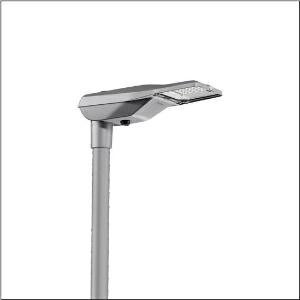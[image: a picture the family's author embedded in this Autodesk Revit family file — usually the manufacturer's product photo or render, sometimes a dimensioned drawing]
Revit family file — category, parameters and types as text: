
# Revit family: streetlight_sl_21_micro___st1_0ab_5xe1m33r08db_c8c0
name_source: partatom
category: Lighting Fixtures
units: mm (PartAtom-declared; Revit-internal decimal feet)

## family parameters
Cut with Voids When Loaded = No
Host = Face
Light Source = No
Part Type = Normal
Room Calculation Point = No
Round Connector Dimension = Use Diameter
Shared = No

## types (1)
- --- (1 x LED, 4500 lm, 39.1 W, 3000K)
    Apparent Load = 39 VA
    CIE Flux Codes = 38 73 97 100 100
    Color Rendering = 70
    Color Temperature = 3000K
    Default Elevation = 1800 mm
    Description = Streetlight SL 21 micro, mast luminaire, primary light control with lens, of PMMA, primary optical cover: cover, of toughened safety glass, transparent, light distribution: ST1.0aB, light emission: direct distribution, primary light characteristic: asymmetric, installation type: side-entry, post-top, LED, High Power LED, rated luminous flux: 4.500lm, luminous efficacy: 115lm/W, light colour: 730, colour temperature: 3000K, control: flexible luminous flux parameterisation, time-dependent luminous flux control, constant luminous flux control, overheat protection, pre-setting: logarithmic dimming characteristic, mains connection: 220..240V, AC, 50/60Hz, start of lifetime: 39W, end of service life: 41W, reduction: 18W, luminaire housing, of diecast aluminium, powder-coated, Siteco® metallic grey (DB 702S), corrosivity category C5 mid according to DIN EN ISO 12944, please order mast flange separately, inclination adjustable: 0°, 5°, 10°, 15°, sealing non-destructively replaceable, multi-level sealing system, length: 528mm, width: 235mm, height: 110mm, mast flange for spigot size: 42mm (side-entry): 5XC10008XM4, 60/48mm (side-entry/post-top): 5XC10108XM2, 76/60mm (side-entry/post-top): 5XC10108XM1, Smart Interface below, protection rating (complete): IP66, insulation class (complete): insulation class II (safety insulation), certification: CE, ENEC, ENEC+, VDE, impact resistance: IK09, permissible operating ambient temperature for outdoor applications: -40..+50°C, standard-compliant lighting for roads and squares, packaging unit: 1 piece

Light Distribution: ST1.0aB
    Height = 110 mm
    Lamp = 1 x LED
    Lamp Light Flux = 4500 lm
    Lamp Power = 39.1 W
    Lamp count = 1
    Length = 528 mm
    Luminous efficacy = 115 lm/W
    Manufacturer = Siteco
    ModVariant = No
    Model = 5XE1M33R08DB
    Number of Poles = 1
    OnlyDefault = Yes
    Power Factor = 1
    Product Name = Streetlight SL 21 micro | ST1.0aB
    Product group = mast luminaire | pylon top
    ProductGroupID = 6100
    Protection Class = Protection class II
    Protection Degree = IP 66
    RLX_Detail_Level = 1
    RLX_Emergency_Light_Flux = 0 lm
    RLX_Emergency_Type = 0
    RLX_Emergency_Type_DB = No
    RlxData = <blob elided: 98525 chars, md5=f1d35da3>
    Socket = socket
    Standby Power = 0 W
    System Light Flux = 4500 lm
    System Power = 39 W
    Type Comments = factory setting: luminous flux: 100 % | dim-lin: 254 | 765 mA
    Type Image = l_1277290.jpg
    URL = http://relux.com
    VarID = @adj_124387
    Voltage = 0 V
    Weight = 0.00 kg
    Width = 235 mm

## geometry (parser evidence)
native form markers: Blend x4, Sweep x9
no freeform markers — native parametric forms only
